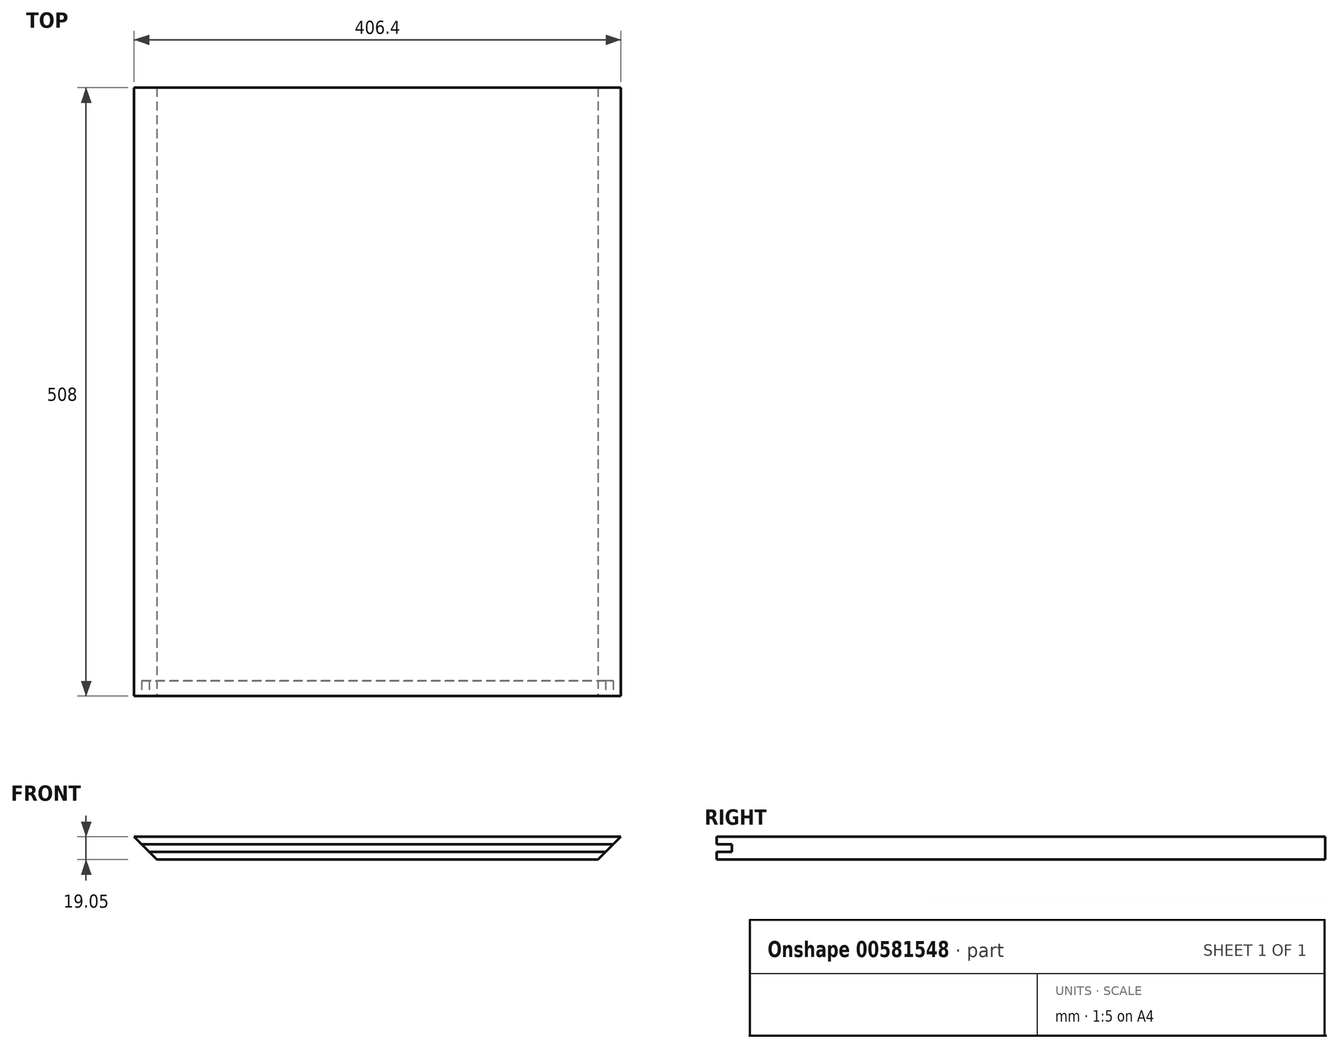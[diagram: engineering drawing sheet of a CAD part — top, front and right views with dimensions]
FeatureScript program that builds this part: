
annotation { "Feature Type Name" : "Feature", "Feature Type Description" : "" }
export const myFeature = defineFeature(function(context is Context, id is Id, definition is map)
    precondition{}
    {
        {
            var Q0;
            Q0=qCreatedBy(makeId("Front.planeOp"),FACE);
            var sketch = newSketch(context, id + "F0", { "sketchPlane" : qUnion([Q0])});
            skLineSegment(sketch, "E0", {"start": v(0, 0) * mm, "end": v(406.4, 0) * mm});
            skLineSegment(sketch, "E1", {"start": v(406.4, 0) * mm, "end": v(387.35, -19.05) * mm});
            skLineSegment(sketch, "E2", {"start": v(387.35, -19.05) * mm, "end": v(19.05, -19.05) * mm});
            skLineSegment(sketch, "E3", {"start": v(19.05, -19.05) * mm, "end": v(0, 0) * mm});
            skSolve(sketch);
        }
        {
            var Q0;
            Q0=makeQuery(id+"F0.imprint","IMPRINT",FACE,{"disambiguationData":[TD([[makeQuery(id+"F0.imprint","IMPRINT",EDGE,{"derivedFrom":sQuery(id+"F0.wireOp",EDGE,"E0")}),-1.0]])]});
            extrude(context, id + "F1", {"entities" : qUnion([Q0]), "oppositeDirection" : true, "depth" : 508 * mm, "offsetDistance" : 25.4 * mm});
        }
        {
            var Q0;
            Q0=makeQuery(id+"F1.opExtrude","CAP_FACE",FACE,{"disambiguationData":[OSD([sQuery(id+"F0.wireOp",EDGE,"E0"),sQuery(id+"F0.wireOp",EDGE,"E1"),sQuery(id+"F0.wireOp",EDGE,"E2"),sQuery(id+"F0.wireOp",EDGE,"E3")])],"isStart":true});
            var sketch = newSketch(context, id + "F2", { "sketchPlane" : qUnion([Q0])});
            skLineSegment(sketch, "E4", {"start": v(6.35, -6.35) * mm, "end": v(400.05, -6.35) * mm});
            skLineSegment(sketch, "E5", {"start": v(400.05, -6.35) * mm, "end": v(400.05, -12.7) * mm});
            skLineSegment(sketch, "E6", {"start": v(400.05, -12.7) * mm, "end": v(6.35, -12.7) * mm});
            skLineSegment(sketch, "E7", {"start": v(6.35, -12.7) * mm, "end": v(6.35, -6.35) * mm});
            skSolve(sketch);
        }
        {
            var Q0;
            {var subQ0=sQuery(id+"F2.wireOp",EDGE,"E4");Q0=makeQuery(id+"F2.imprint","IMPRINT",FACE,{"disambiguationData":[TD([[makeQuery(id+"F2.imprint","IMPRINT",EDGE,{"derivedFrom":subQ0}),-1.0]])]});}
            extrude(context, id + "F3", {"entities" : qUnion([Q0]), "operationType" : NewBodyOperationType.REMOVE, "oppositeDirection" : true, "depth" : 12.7 * mm, "offsetDistance" : 25.4 * mm});
        }
    });
